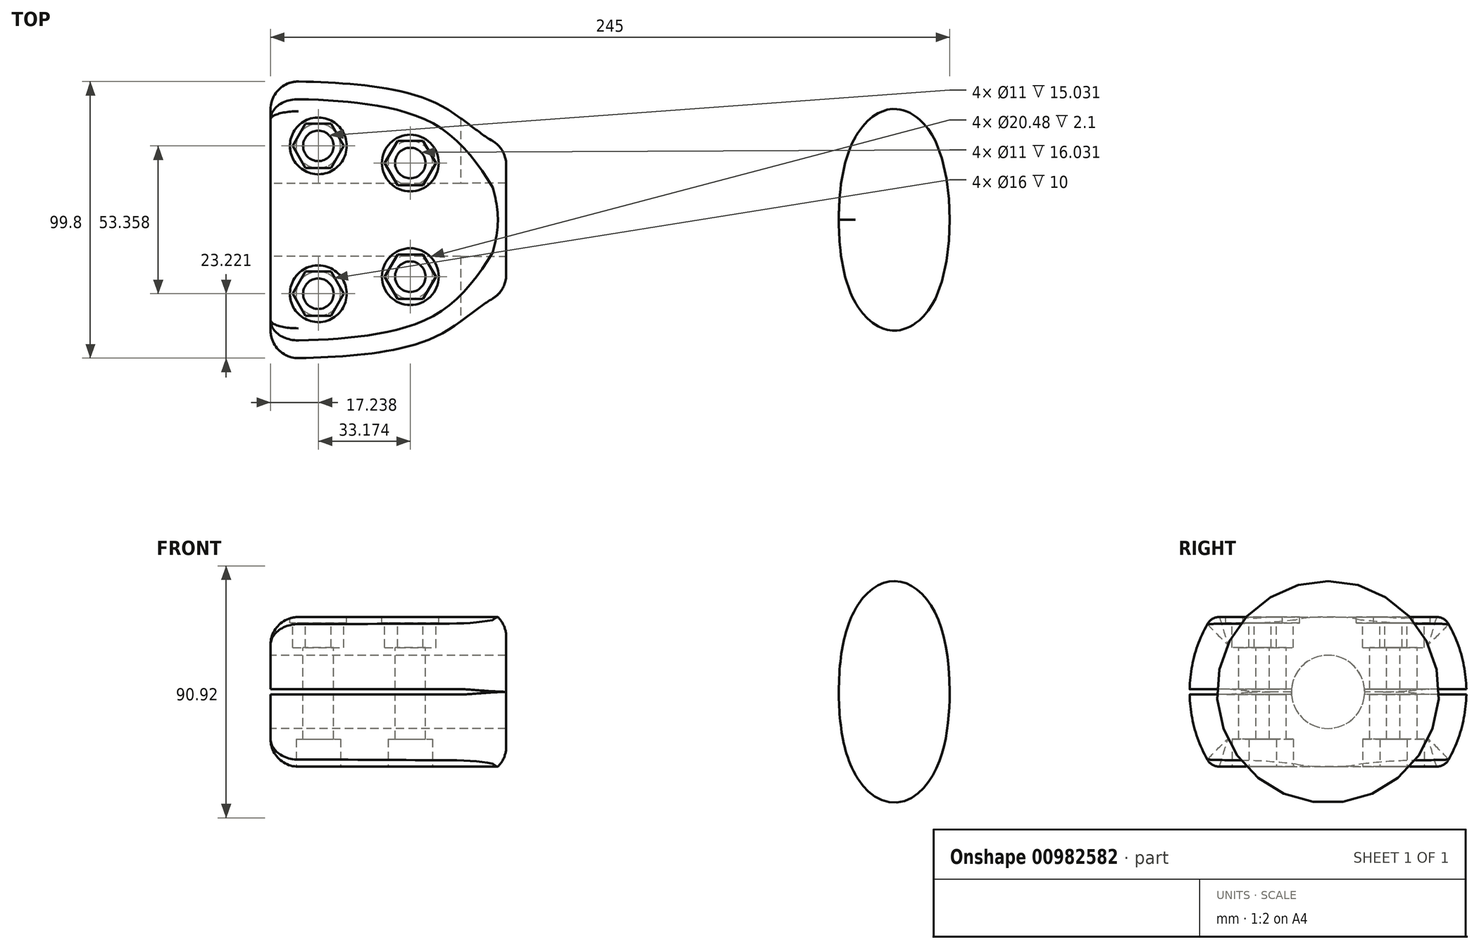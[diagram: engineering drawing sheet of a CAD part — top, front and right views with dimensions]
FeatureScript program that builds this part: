
annotation { "Feature Type Name" : "Feature", "Feature Type Description" : "" }
export const myFeature = defineFeature(function(context is Context, id is Id, definition is map)
    precondition{}
    {
        {
            var Q0;
            Q0=qCreatedBy(makeId("Front.planeOp"),FACE);
            var sketch = newSketch(context, id + "F0", { "sketchPlane" : qUnion([Q0])});
            skLineSegment(sketch, "E0", {"start": v(0, 50) * mm, "end": v(0, 0) * mm});
            skLineSegment(sketch, "E1", {"start": v(0, 0) * mm, "end": v(245, 0) * mm});
            skLineSegment(sketch, "E2", {"start": v(85, 0) * mm, "end": v(85, 26) * mm, "construction": true});
            skLineSegment(sketch, "E3", {"start": v(145, 0) * mm, "end": v(145, 24) * mm, "construction": true});
            skLineSegment(sketch, "E4", {"start": v(205, 0) * mm, "end": v(205, 22) * mm, "construction": true});
            skLineSegment(sketch, "E5", {"start": v(225, 0) * mm, "end": v(225, 40) * mm, "construction": true});
            skLineSegment(sketch, "E6", {"start": v(60, 42) * mm, "end": v(60, 0) * mm, "construction": true});
            skFitSpline(sketch, "E7", {"points": [v(0, 50) * mm, v(60, 42) * mm, v(85, 26) * mm, v(145, 24) * mm, v(205, 22) * mm], "startDerivative": vector(265.83, 0) * mm, "endDerivative": vector(46.66, -3.23) * mm, "construction": true});
            skLineSegment(sketch, "E8", {"start": v(85, 26) * mm, "end": v(85, 0) * mm});
            skLineSegment(sketch, "E9", {"start": v(0, 0) * mm, "end": v(85, 0) * mm});
            skLineSegment(sketch, "E10", {"start": v(205, 22) * mm, "end": v(205, 0) * mm});
            skLineSegment(sketch, "E11", {"start": v(245, 0) * mm, "end": v(205, 0) * mm});
            skLineSegment(sketch, "E12.top", {"start": v(211, 0) * mm, "end": v(239, 0) * mm});
            skFitSpline(sketch, "E13", {"points": [v(196, 22.57) * mm, v(205, 24.2) * mm, v(211.85, 31.36) * mm], "startDerivative": vector(27.96, -1.73) * mm, "endDerivative": vector(11.53, 20.5) * mm});
            skLineSegment(sketch, "E14.bottom", {"start": v(237, 33) * mm, "end": v(213, 33) * mm, "construction": true});
            skLineSegment(sketch, "E14.top", {"start": v(237, -33) * mm, "end": v(213, -33) * mm, "construction": true});
            skLineSegment(sketch, "E14.left", {"start": v(237, 33) * mm, "end": v(237, -33) * mm, "construction": true});
            skLineSegment(sketch, "E14.right", {"start": v(213, 33) * mm, "end": v(213, -33) * mm, "construction": true});
            skPoint(sketch, "E14.middle", {"position": v(225, 0) * mm});
            skLineSegment(sketch, "E15.bottom", {"start": v(239, 0) * mm, "end": v(245, 0) * mm});
            skLineSegment(sketch, "E16.bottom", {"start": v(245, 15) * mm, "end": v(205, 15) * mm, "construction": true});
            skLineSegment(sketch, "E16.top", {"start": v(245, 0) * mm, "end": v(205, 0) * mm, "construction": true});
            skLineSegment(sketch, "E16.right", {"start": v(205, 15) * mm, "end": v(205, 0) * mm, "construction": true});
            skFitSpline(sketch, "E17", {"points": [v(245, 0) * mm, v(237, 33) * mm, v(225, 40) * mm, v(213, 33) * mm, v(205, 0) * mm], "startDerivative": vector(0, 147.57) * mm, "endDerivative": vector(-0.02, -147.57) * mm});
            skFitSpline(sketch, "E18", {"points": [v(0, 50) * mm, v(60, 42) * mm, v(85, 26) * mm, v(145, 23) * mm, v(205, 24) * mm], "startDerivative": vector(265.83, 0) * mm, "endDerivative": vector(46.28, 3.62) * mm});
            skLineSegment(sketch, "E19", {"start": v(170.4, -9.3) * mm, "end": v(237.63, 57.93) * mm, "construction": true});
            skFitSpline(sketch, "E20", {"points": [v(194.65, 23.79) * mm, v(215, 35.3) * mm], "startDerivative": vector(27, 0.47) * mm, "endDerivative": vector(19.11, 19.11) * mm, "construction": true});
            skSolve(sketch);
        }
        {
            var Q0;
            {var subQ0=sQuery(id+"F0.wireOp",EDGE,"E0");Q0=makeQuery(id+"F0.imprint","IMPRINT",FACE,{"disambiguationData":[TD([[makeQuery(id+"F0.imprint","IMPRINT",EDGE,{"derivedFrom":subQ0}),1.0]])]});}
            var Q1;
            Q1=makeQuery(id+"F0.imprint","IMPRINT",FACE,{"disambiguationData":[TD([[makeQuery(id+"F0.imprint","IMPRINT",EDGE,{"derivedFrom":sQuery(id+"F0.wireOp",EDGE,"27aa72ab-a35f-4556-a79f-be58b9bce097")}),-1.0]])]});
            var Q2;
            Q2=makeQuery(id+"F0.imprint","IMPRINT",FACE,{"disambiguationData":[TD([[makeQuery(id+"F0.imprint","IMPRINT",EDGE,{"derivedFrom":sQuery(id+"F0.wireOp",EDGE,"E1")}),1.0]])]});
            var Q3;
            {var subQ0=sQuery(id+"F0.wireOp",EDGE,"d97d6b34-898e-417b-85eb-bfbc859b7b58");var subQ4=sQuery(id+"F0.wireOp",EDGE,"E11");var subQ5=makeQuery(id+"F0.imprint","INTERSECT",VERTEX,{"disambiguationData":[OD(0.0)],"derivedFrom":[subQ4,subQ0]});Q3=makeQuery(id+"F0.imprint","IMPRINT",FACE,{"disambiguationData":[TD([[makeQuery(id+"F0.imprint","IMPRINT",EDGE,{"disambiguationData":[TD([[subQ5,-1.0]])],"derivedFrom":subQ4}),-1.0]])]});}
            var Q4;
            {var subQ0=sQuery(id+"F0.wireOp",EDGE,"E10");Q4=makeQuery(id+"F0.imprint","IMPRINT",FACE,{"disambiguationData":[TD([[makeQuery(id+"F0.imprint","IMPRINT",EDGE,{"derivedFrom":subQ0}),1.0]])]});}
            var Q5;
            Q5=sQuery(id+"F0.wireOp",EDGE,"E1");
            revolve(context, id + "F1", {"surfaceOperationType" : NewSurfaceOperationType.NEW, "entities" : qUnion([Q0, Q1, Q2, Q3, Q4]), "axis" : qUnion([Q5]), "revolveType" : RevolveType.FULL});
        }
        {
            var Q0;
            Q0=qCreatedBy(makeId("Right.planeOp"),FACE);
            cPlane(context, id + "F2", {"entities" : qUnion([Q0]), "cplaneType" : CPlaneType.OFFSET, "offset" : 90 * mm, "width" : 150 * mm, "height" : 150 * mm});
        }
        {
            var Q0;
            Q0=qCreatedBy(id+"F2.planeOp",FACE);
            var sketch = newSketch(context, id + "F3", { "sketchPlane" : qUnion([Q0])});
            skLineSegment(sketch, "E21.bottom", {"start": v(-65.87, 27) * mm, "end": v(58.89, 27) * mm});
            skLineSegment(sketch, "E21.top", {"start": v(-65.87, -27) * mm, "end": v(58.89, -27) * mm});
            skLineSegment(sketch, "E21.left", {"start": v(-65.87, 27) * mm, "end": v(-65.87, -27) * mm});
            skLineSegment(sketch, "E21.right", {"start": v(58.89, 27) * mm, "end": v(58.89, -27) * mm});
            skPoint(sketch, "E21.middle", {"position": v(-3.5, 0) * mm});
            skLineSegment(sketch, "E22.bottom", {"start": v(-135.82, 62.52) * mm, "end": v(135.82, 62.52) * mm});
            skLineSegment(sketch, "E22.top", {"start": v(-135.82, -80.38) * mm, "end": v(135.82, -80.38) * mm});
            skLineSegment(sketch, "E22.left", {"start": v(-135.82, 62.52) * mm, "end": v(-135.82, -80.38) * mm});
            skLineSegment(sketch, "E22.right", {"start": v(135.82, 62.52) * mm, "end": v(135.82, -80.38) * mm});
            skPoint(sketch, "E22.middle", {"position": v(0, -8.93) * mm});
            skSolve(sketch);
        }
        {
            var Q0;
            Q0=makeQuery(id+"F3.imprint","IMPRINT",FACE,{"disambiguationData":[TD([[makeQuery(id+"F3.imprint","IMPRINT",EDGE,{"derivedFrom":sQuery(id+"F3.wireOp",EDGE,"E21.bottom")}),1.0]])]});
            extrude(context, id + "F4", {"entities" : qUnion([Q0]), "operationType" : NewBodyOperationType.REMOVE, "oppositeDirection" : true, "depth" : 139 * mm, "offsetDistance" : 25 * mm});
        }
        {
            var Q0;
            Q0=makeQuery(id+"F4.boolean.opBoolean","INTERSECT",EDGE,{"derivedFrom":[makeQuery(id+"F1.opRevolve","SWEPT_FACE",FACE,{"disambiguationData":[OSD([sQuery(id+"F0.wireOp",EDGE,"E18")])]}),makeQuery(id+"F4.opExtrude","SWEPT_FACE",FACE,{"disambiguationData":[OSD([sQuery(id+"F3.wireOp",EDGE,"E21.bottom")])]})]});
            var Q1;
            Q1=makeQuery(id+"F4.boolean.opBoolean","INTERSECT",EDGE,{"derivedFrom":[makeQuery(id+"F1.opRevolve","SWEPT_FACE",FACE,{"disambiguationData":[OSD([sQuery(id+"F0.wireOp",EDGE,"E18")])]}),makeQuery(id+"F4.opExtrude","SWEPT_FACE",FACE,{"disambiguationData":[OSD([sQuery(id+"F3.wireOp",EDGE,"E21.top")])]})]});
            fillet(context, id + "F5", {"entities" : qUnion([Q0, Q1]), "radius" : 5 * mm, "tangentPropagation" : true, "allowEdgeOverflow" : false});
        }
        {
            var Q0;
            Q0=makeQuery(id+"F4.boolean.opBoolean","COPY",FACE,{"derivedFrom":makeQuery(id+"F4.opExtrude","SWEPT_FACE",FACE,{"disambiguationData":[OSD([sQuery(id+"F3.wireOp",EDGE,"E21.bottom")])]})});
            var sketch = newSketch(context, id + "F6", { "sketchPlane" : qUnion([Q0])});
            skLineSegment(sketch, "E23", {"start": v(0, 0) * mm, "end": v(79.24, 0) * mm, "construction": true});
            skCircle(sketch, "E24.cCircle", {"center": v(50.41, 20.5) * mm, "radius": 8 * mm, "construction": true});
            skLineSegment(sketch, "E24.0", {"start": v(55.03, 28.5) * mm, "end": v(59.65, 20.5) * mm});
            skLineSegment(sketch, "E24.1", {"start": v(59.65, 20.5) * mm, "end": v(55.03, 12.5) * mm});
            skLineSegment(sketch, "E24.2", {"start": v(55.03, 12.5) * mm, "end": v(45.8, 12.5) * mm});
            skLineSegment(sketch, "E24.3", {"start": v(45.8, 12.5) * mm, "end": v(41.17, 20.5) * mm});
            skLineSegment(sketch, "E24.4", {"start": v(41.17, 20.5) * mm, "end": v(45.8, 28.5) * mm});
            skLineSegment(sketch, "E24.5", {"start": v(45.8, 28.5) * mm, "end": v(55.03, 28.5) * mm});
            skPoint(sketch, "E24.0.midPoint", {"position": v(57.34, 24.5) * mm});
            skCircle(sketch, "E25.cCircle", {"center": v(17.24, 26.68) * mm, "radius": 8 * mm, "construction": true});
            skLineSegment(sketch, "E25.0", {"start": v(12.62, 34.68) * mm, "end": v(21.86, 34.68) * mm});
            skLineSegment(sketch, "E25.1", {"start": v(21.86, 34.68) * mm, "end": v(26.48, 26.68) * mm});
            skLineSegment(sketch, "E25.2", {"start": v(26.48, 26.68) * mm, "end": v(21.86, 18.68) * mm});
            skLineSegment(sketch, "E25.3", {"start": v(21.86, 18.68) * mm, "end": v(12.62, 18.68) * mm});
            skLineSegment(sketch, "E25.4", {"start": v(12.62, 18.68) * mm, "end": v(8, 26.68) * mm});
            skLineSegment(sketch, "E25.5", {"start": v(8, 26.68) * mm, "end": v(12.62, 34.68) * mm});
            skPoint(sketch, "E25.0.midPoint", {"position": v(17.24, 34.68) * mm});
            skPoint(sketch, "E26.cCircle.perimeterSnap0", {"position": v(24.17, 30.68) * mm});
            skPoint(sketch, "E26.0.midPoint.positionSnap0", {"position": v(24.17, 30.68) * mm});
            skCircle(sketch, "E27", {"center": v(17.24, 26.68) * mm, "radius": 10.24 * mm, "construction": true});
            skCircle(sketch, "E28", {"center": v(50.41, 20.5) * mm, "radius": 10.24 * mm, "construction": true});
            skFitSpline(sketch, "E29.0", {"points": [v(0, -39.25) * mm, v(2.09, -39.33) * mm, v(6.26, -39.44) * mm, v(12.52, -39.44) * mm, v(18.78, -39.26) * mm, v(23.99, -38.94) * mm, v(28.15, -38.55) * mm, v(32.3, -38.07) * mm, v(36.42, -37.45) * mm, v(40.5, -36.65) * mm, v(43.55, -35.94) * mm, v(46.07, -35.26) * mm, v(48.07, -34.64) * mm, v(50.05, -33.97) * mm, v(52.49, -33.05) * mm, v(55.32, -31.77) * mm, v(58.05, -30.29) * mm, v(60.22, -28.85) * mm, v(61.9, -27.58) * mm, v(63.54, -26.26) * mm, v(65.5, -24.52) * mm, v(67.73, -22.34) * mm, v(69.9, -20.1) * mm, v(72.02, -17.8) * mm, v(74.12, -15.49) * mm, v(76.2, -13.16) * mm, v(78.24, -10.8) * mm, v(79.9, -8.8) * mm, v(81.17, -7.13) * mm, v(82.08, -5.84) * mm, v(82.9, -4.48) * mm, v(83.47, -3.3) * mm, v(83.83, -2.3) * mm, v(84.1, -1.27) * mm, v(84.2, -0.23) * mm, v(84.14, 0.84) * mm, v(84.01, 1.62) * mm, v(83.8, 2.38) * mm, v(83.53, 3.13) * mm, v(83.2, 3.85) * mm, v(82.72, 4.78) * mm, v(82.04, 5.9) * mm, v(81.14, 7.18) * mm, v(79.86, 8.85) * mm, v(78.19, 10.87) * mm, v(76.12, 13.24) * mm, v(74.03, 15.58) * mm, v(71.93, 17.9) * mm, v(69.8, 20.2) * mm, v(67.61, 22.46) * mm, v(65.36, 24.65) * mm, v(63.4, 26.38) * mm, v(61.75, 27.7) * mm, v(60.47, 28.65) * mm, v(59.16, 29.55) * mm, v(57.38, 30.65) * mm, v(55.1, 31.88) * mm, v(52.26, 33.14) * mm, v(48.39, 34.6) * mm, v(44.4, 35.75) * mm, v(40.3, 36.7) * mm, v(37.23, 37.29) * mm, v(34.15, 37.8) * mm, v(30.04, 38.36) * mm, v(24.89, 38.88) * mm, v(18.69, 39.27) * mm, v(12.47, 39.45) * mm, v(6.24, 39.44) * mm, v(2.08, 39.33) * mm, v(0, 39.25) * mm]});
            skLineSegment(sketch, "E30", {"start": v(55.49, 29.39) * mm, "end": v(56.42, 31.16) * mm, "construction": true});
            skLineSegment(sketch, "E31", {"start": v(17.3, 36.92) * mm, "end": v(17.3, 38.92) * mm, "construction": true});
            skCircle(sketch, "E32", {"center": v(50.41, 20.5) * mm, "radius": 5.5 * mm, "construction": true});
            skLineSegment(sketch, "E33.MirrorCS", {"start": v(55.49, -29.39) * mm, "end": v(56.42, -31.16) * mm, "construction": true});
            skLineSegment(sketch, "E34.MirrorCS", {"start": v(17.3, -36.92) * mm, "end": v(17.3, -38.92) * mm, "construction": true});
            skLineSegment(sketch, "E35.MirrorCS", {"start": v(12.62, -34.68) * mm, "end": v(21.86, -34.68) * mm});
            skLineSegment(sketch, "E36.MirrorCS", {"start": v(21.86, -34.68) * mm, "end": v(26.48, -26.68) * mm});
            skLineSegment(sketch, "E37.MirrorCS", {"start": v(45.8, -28.5) * mm, "end": v(55.03, -28.5) * mm});
            skPoint(sketch, "E38.MirrorP", {"position": v(24.17, -30.68) * mm});
            skLineSegment(sketch, "E39.MirrorCS", {"start": v(26.48, -26.68) * mm, "end": v(21.86, -18.68) * mm});
            skLineSegment(sketch, "E40.MirrorCS", {"start": v(41.17, -20.5) * mm, "end": v(45.8, -28.5) * mm});
            skLineSegment(sketch, "E41.MirrorCS", {"start": v(21.86, -18.68) * mm, "end": v(12.62, -18.68) * mm});
            skLineSegment(sketch, "E42.MirrorCS", {"start": v(8, -26.68) * mm, "end": v(12.62, -34.68) * mm});
            skLineSegment(sketch, "E43.MirrorCS", {"start": v(12.62, -18.68) * mm, "end": v(8, -26.68) * mm});
            skLineSegment(sketch, "E44.MirrorCS", {"start": v(55.03, -28.5) * mm, "end": v(59.65, -20.5) * mm});
            skLineSegment(sketch, "E45.MirrorCS", {"start": v(59.65, -20.5) * mm, "end": v(55.03, -12.5) * mm});
            skCircle(sketch, "E46.MirrorC", {"center": v(17.24, -26.68) * mm, "radius": 10.24 * mm, "construction": true});
            skLineSegment(sketch, "E47.MirrorCS", {"start": v(55.03, -12.5) * mm, "end": v(45.8, -12.5) * mm});
            skCircle(sketch, "E48.MirrorC", {"center": v(17.24, -26.68) * mm, "radius": 8 * mm, "construction": true});
            skCircle(sketch, "E49.MirrorC", {"center": v(50.41, -20.5) * mm, "radius": 5.5 * mm, "construction": true});
            skCircle(sketch, "E50.MirrorC", {"center": v(50.41, -20.5) * mm, "radius": 8 * mm, "construction": true});
            skPoint(sketch, "E51.MirrorP", {"position": v(57.34, -24.5) * mm});
            skCircle(sketch, "E52.MirrorC", {"center": v(50.41, -20.5) * mm, "radius": 10.24 * mm, "construction": true});
            skPoint(sketch, "E53.MirrorP", {"position": v(17.24, -34.68) * mm});
            skLineSegment(sketch, "E54.MirrorCS", {"start": v(45.8, -12.5) * mm, "end": v(41.17, -20.5) * mm});
            skSolve(sketch);
        }
        {
            var Q0;
            Q0=qSketchRegion(id+"F6",true);
            extrude(context, id + "F7", {"entities" : qUnion([Q0]), "operationType" : NewBodyOperationType.REMOVE, "oppositeDirection" : true, "depth" : 11 * mm, "offsetDistance" : 25 * mm});
        }
        {
            var Q0;
            Q0=makeQuery(id+"F4.boolean.opBoolean","COPY",FACE,{"derivedFrom":makeQuery(id+"F4.opExtrude","SWEPT_FACE",FACE,{"disambiguationData":[OSD([sQuery(id+"F3.wireOp",EDGE,"E21.bottom")])]})});
            var sketch = newSketch(context, id + "F8", { "sketchPlane" : qUnion([Q0])});
            skCircle(sketch, "E55.20", {"center": v(17.24, 26.68) * mm, "radius": 10.24 * mm});
            skCircle(sketch, "E55.21", {"center": v(50.41, 20.5) * mm, "radius": 10.24 * mm});
            skLineSegment(sketch, "E56", {"start": v(0, 0) * mm, "end": v(81.65, 0) * mm, "construction": true});
            skCircle(sketch, "E57.MirrorC", {"center": v(17.24, -26.68) * mm, "radius": 10.24 * mm});
            skCircle(sketch, "E58.MirrorC", {"center": v(50.41, -20.5) * mm, "radius": 10.24 * mm});
            skSolve(sketch);
        }
        {
            var Q0;
            Q0=qSketchRegion(id+"F8",true);
            extrude(context, id + "F9", {"entities" : qUnion([Q0]), "operationType" : NewBodyOperationType.REMOVE, "oppositeDirection" : true, "depth" : 2.1 * mm, "offsetDistance" : 25 * mm});
        }
        {
            var Q0;
            Q0=makeQuery(id+"F4.boolean.opBoolean","COPY",FACE,{"derivedFrom":makeQuery(id+"F4.opExtrude","SWEPT_FACE",FACE,{"disambiguationData":[OSD([sQuery(id+"F3.wireOp",EDGE,"E21.bottom")])]})});
            var sketch = newSketch(context, id + "F10", { "sketchPlane" : qUnion([Q0])});
            skCircle(sketch, "E59.0", {"center": v(17.24, 26.68) * mm, "radius": 10.24 * mm, "construction": true});
            skCircle(sketch, "E60.0", {"center": v(50.41, 20.5) * mm, "radius": 10.24 * mm, "construction": true});
            skCircle(sketch, "E61", {"center": v(17.24, 26.68) * mm, "radius": 5.5 * mm});
            skCircle(sketch, "E62", {"center": v(50.41, 20.5) * mm, "radius": 5.5 * mm});
            skLineSegment(sketch, "E63", {"start": v(0, 0) * mm, "end": v(81.65, 0) * mm, "construction": true});
            skCircle(sketch, "E64.MirrorC", {"center": v(17.24, -26.68) * mm, "radius": 5.5 * mm});
            skCircle(sketch, "E65.MirrorC", {"center": v(50.41, -20.5) * mm, "radius": 5.5 * mm});
            skSolve(sketch);
        }
        {
            var Q0;
            Q0=qSketchRegion(id+"F10",true);
            extrude(context, id + "F11", {"entities" : qUnion([Q0]), "operationType" : NewBodyOperationType.REMOVE, "endBound" : BoundingType.THROUGH_ALL, "oppositeDirection" : true, "depth" : 25 * mm, "offsetDistance" : 25 * mm});
        }
        {
            var Q0;
            Q0=makeQuery(id+"F4.boolean.opBoolean","COPY",FACE,{"derivedFrom":makeQuery(id+"F4.opExtrude","SWEPT_FACE",FACE,{"disambiguationData":[OSD([sQuery(id+"F3.wireOp",EDGE,"E21.top")])]})});
            var sketch = newSketch(context, id + "F12", { "sketchPlane" : qUnion([Q0])});
            skCircle(sketch, "E66.0", {"center": v(50.41, -20.5) * mm, "radius": 5.5 * mm, "construction": true});
            skCircle(sketch, "E66.1", {"center": v(17.24, -26.68) * mm, "radius": 5.5 * mm, "construction": true});
            skCircle(sketch, "E66.2", {"center": v(17.24, -26.68) * mm, "radius": 5.5 * mm, "construction": true});
            skCircle(sketch, "E66.3", {"center": v(17.24, -26.68) * mm, "radius": 5.5 * mm, "construction": true});
            skCircle(sketch, "E67", {"center": v(17.24, -26.68) * mm, "radius": 8 * mm});
            skCircle(sketch, "E68", {"center": v(50.41, -20.5) * mm, "radius": 8 * mm});
            skLineSegment(sketch, "E69", {"start": v(0, 0) * mm, "end": v(81.65, 0) * mm, "construction": true});
            skLineSegment(sketch, "E70", {"start": v(81.65, 0) * mm, "end": v(79.9, 1.17) * mm, "construction": true});
            skCircle(sketch, "E71.MirrorC", {"center": v(17.24, 26.68) * mm, "radius": 8 * mm});
            skCircle(sketch, "E72.MirrorC", {"center": v(50.41, 20.5) * mm, "radius": 8 * mm});
            skSolve(sketch);
        }
        {
            var Q0;
            Q0=qSketchRegion(id+"F12",true);
            extrude(context, id + "F13", {"entities" : qUnion([Q0]), "operationType" : NewBodyOperationType.REMOVE, "oppositeDirection" : true, "depth" : 10 * mm, "offsetDistance" : 25 * mm});
        }
        {
            var Q0;
            Q0=qCreatedBy(makeId("Front.planeOp"),FACE);
            var sketch = newSketch(context, id + "F14", { "sketchPlane" : qUnion([Q0])});
            skLineSegment(sketch, "E73.bottom", {"start": v(68.64, 0.97) * mm, "end": v(-85.25, 0.97) * mm});
            skLineSegment(sketch, "E73.top", {"start": v(68.64, -0.97) * mm, "end": v(-84.75, -0.97) * mm});
            skLineSegment(sketch, "E73.right", {"start": v(-85.25, 0.97) * mm, "end": v(-84.75, -0.97) * mm});
            skPoint(sketch, "E73.middle", {"position": v(0, 0) * mm});
            skLineSegment(sketch, "E74", {"start": v(0, 0) * mm, "end": v(85, 0) * mm, "construction": true});
            skFitSpline(sketch, "E75", {"points": [v(85, 0) * mm, v(68.64, -0.97) * mm], "startDerivative": vector(-18.41, -0.23) * mm, "endDerivative": vector(-7.17, 0.11) * mm});
            skFitSpline(sketch, "E76.MirrorCS", {"points": [v(85, 0) * mm, v(68.64, 0.97) * mm], "startDerivative": vector(-18.41, 0.23) * mm, "endDerivative": vector(-7.17, -0.11) * mm});
            skPoint(sketch, "E77.orphan", {"position": v(85.25, -0.97) * mm});
            skPoint(sketch, "E73.left.start.orphan", {"position": v(84.75, 0.97) * mm});
            skSolve(sketch);
        }
        {
            var Q0;
            Q0=qSketchRegion(id+"F14",true);
            extrude(context, id + "F15", {"entities" : qUnion([Q0]), "operationType" : NewBodyOperationType.REMOVE, "endBound" : BoundingType.SYMMETRIC, "oppositeDirection" : true, "depth" : 120 * mm, "offsetDistance" : 25 * mm});
        }
        {
            var Q0;
            {var subQ1=sQuery(id+"F3.wireOp",EDGE,"E21.top");Q0=makeQuery(id+"F15.boolean.opBoolean","SPLIT",FACE,{"disambiguationData":[TD([makeQuery(id+"F4.boolean.opBoolean","COPY",FACE,{"derivedFrom":makeQuery(id+"F4.opExtrude","SWEPT_FACE",FACE,{"disambiguationData":[OSD([subQ1])]})})])],"derivedFrom":makeQuery(id+"F1.opRevolve","SWEPT_FACE",FACE,{"disambiguationData":[OSD([sQuery(id+"F0.wireOp",EDGE,"E0")])]})});}
            var sketch = newSketch(context, id + "F16", { "sketchPlane" : qUnion([Q0])});
            skCircle(sketch, "E78", {"center": v(0, 0) * mm, "radius": 13.2 * mm});
            skSolve(sketch);
        }
        {
            var Q0;
            Q0=qSketchRegion(id+"F16",true);
            extrude(context, id + "F17", {"entities" : qUnion([Q0]), "operationType" : NewBodyOperationType.REMOVE, "oppositeDirection" : true, "depth" : 130 * mm, "offsetDistance" : 25 * mm});
        }
        {
            var Q0;
            Q0=makeQuery(id+"F1.opRevolve","SWEPT_EDGE",EDGE,{"disambiguationData":[OSD([sQuery(id+"F0.wireOp",EDGE,"E13"),sQuery(id+"F0.wireOp",EDGE,"E18")])]});
            fillet(context, id + "F18", {"entities" : qUnion([Q0]), "radius" : 10 * mm, "tangentPropagation" : true, "allowEdgeOverflow" : false});
        }
    });
